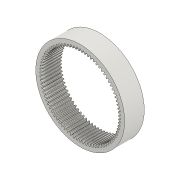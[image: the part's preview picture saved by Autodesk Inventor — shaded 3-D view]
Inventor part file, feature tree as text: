
AUTODESK INVENTOR PART (.ipt)
format: ipt  version: 2020.3 (Build 243373010, 373A)  size: 489,984 bytes
history: native  units: mm (DEFAULTED — no unit token found)
features: plane x3, other x3, sketch x2, extrude x1
ambient origin geometry x8: Origin, YZ Plane, XZ Plane, XY Plane, X Axis, Y Axis, Z Axis, Center Point
bodies: Solid1 (feature_tree)
feature tree (9):
  extrude  "Extrusion1"  Depth=10.0mm TaperAngle=0.0deg
  plane  "Work Plane2"
  plane  "Work Plane8"
  plane  "Work Plane9"
  other  "Spur Gear"
  sketch  "Sketch1"  dims[d0=45.375mm d1=10.0mm d2=0.0mm]
  sketch  "Sketch2"  dims[d3=40.0mm d4=10.0mm d5=0.0mm d16=13.75mm d17=0.0mm d34=0.392699mm d39=0.0mm d45=0.0mm d47=13.75mm d50=0.0mm d51=0.0mm d52=13.75mm]
  other  "Srf1"
  other  "Pitch Diameter"
